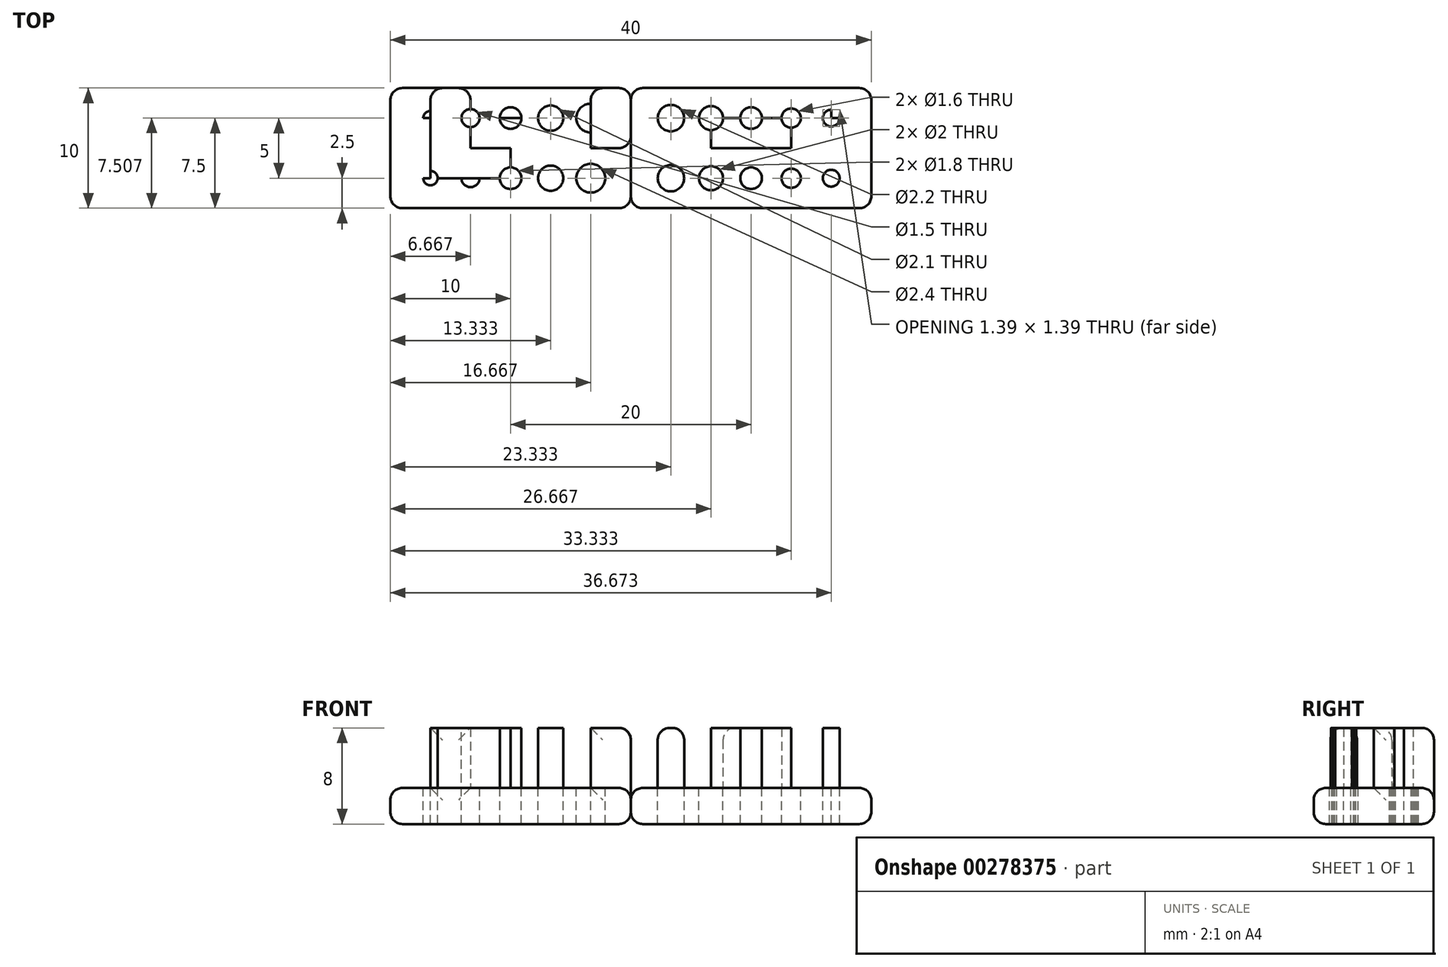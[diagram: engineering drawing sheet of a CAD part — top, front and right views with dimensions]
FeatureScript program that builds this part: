
annotation { "Feature Type Name" : "Feature", "Feature Type Description" : "" }
export const myFeature = defineFeature(function(context is Context, id is Id, definition is map)
    precondition{}
    {
        {
            var Q0;
            Q0=qCreatedBy(makeId("Top.planeOp"),FACE);
            var sketch = newSketch(context, id + "F0", { "sketchPlane" : qUnion([Q0])});
            skLineSegment(sketch, "E0.bottom", {"start": v(10, 2.5) * mm, "end": v(-10, 2.5) * mm});
            skLineSegment(sketch, "E0.top", {"start": v(10, -2.5) * mm, "end": v(-10, -2.5) * mm});
            skLineSegment(sketch, "E0.left", {"start": v(10, 2.5) * mm, "end": v(10, -2.5) * mm});
            skLineSegment(sketch, "E0.right", {"start": v(-10, 2.5) * mm, "end": v(-10, -2.5) * mm});
            skPoint(sketch, "E0.middle", {"position": v(0, 0) * mm});
            skCircle(sketch, "E1", {"center": v(0, 0) * mm, "radius": 0.9 * mm});
            skLineSegment(sketch, "E2", {"start": v(0, 2.5) * mm, "end": v(0, -2.5) * mm});
            skLineSegment(sketch, "E3", {"start": v(-10, 0) * mm, "end": v(10, 0) * mm});
            skLineSegment(sketch, "E4", {"start": v(-6.67, 2.5) * mm, "end": v(-6.67, -2.5) * mm});
            skLineSegment(sketch, "E5", {"start": v(-3.33, 2.5) * mm, "end": v(-3.33, -2.5) * mm});
            skLineSegment(sketch, "E6", {"start": v(3.33, 2.5) * mm, "end": v(3.33, -2.5) * mm});
            skLineSegment(sketch, "E7", {"start": v(6.67, 2.5) * mm, "end": v(6.67, -2.5) * mm});
            skCircle(sketch, "E8", {"center": v(-6.67, 0) * mm, "radius": 0.6 * mm});
            skCircle(sketch, "E9", {"center": v(-3.33, 0) * mm, "radius": 0.75 * mm});
            skCircle(sketch, "E10", {"center": v(3.33, 0) * mm, "radius": 1.05 * mm});
            skCircle(sketch, "E11", {"center": v(6.67, 0) * mm, "radius": 1.2 * mm});
            skLineSegment(sketch, "E12", {"start": v(10, -2.5) * mm, "end": v(10, -7.5) * mm});
            skLineSegment(sketch, "E13", {"start": v(10, -7.5) * mm, "end": v(-10, -7.5) * mm});
            skLineSegment(sketch, "E14", {"start": v(-10, -7.5) * mm, "end": v(-10, -2.5) * mm});
            skLineSegment(sketch, "E15.MirrorCS", {"start": v(-6.67, -7.5) * mm, "end": v(-6.67, -2.5) * mm});
            skLineSegment(sketch, "E16.MirrorCS", {"start": v(-3.33, -7.5) * mm, "end": v(-3.33, -2.5) * mm});
            skLineSegment(sketch, "E17.MirrorCS", {"start": v(0, -7.5) * mm, "end": v(0, -2.5) * mm});
            skLineSegment(sketch, "E18.MirrorCS", {"start": v(3.33, -7.5) * mm, "end": v(3.33, -2.5) * mm});
            skLineSegment(sketch, "E19.MirrorCS", {"start": v(6.67, -7.5) * mm, "end": v(6.67, -2.5) * mm});
            skLineSegment(sketch, "E20.MirrorCS", {"start": v(-10, -5) * mm, "end": v(10, -5) * mm});
            skCircle(sketch, "E21.MirrorC", {"center": v(-6.67, -5) * mm, "radius": 0.6 * mm});
            skCircle(sketch, "E22.MirrorC", {"center": v(-3.33, -5) * mm, "radius": 0.75 * mm});
            skCircle(sketch, "E23.MirrorC", {"center": v(0, -5) * mm, "radius": 0.9 * mm});
            skCircle(sketch, "E24.MirrorC", {"center": v(3.33, -5) * mm, "radius": 1.05 * mm});
            skCircle(sketch, "E25.MirrorC", {"center": v(6.67, -5) * mm, "radius": 1.2 * mm});
            skLineSegment(sketch, "E26.MirrorCS", {"start": v(30, 0) * mm, "end": v(26.67, 0) * mm});
            skLineSegment(sketch, "E27.MirrorCS", {"start": v(10, -2.5) * mm, "end": v(30, -2.5) * mm});
            skLineSegment(sketch, "E28.MirrorCS", {"start": v(10, 2.5) * mm, "end": v(30, 2.5) * mm});
            skLineSegment(sketch, "E29.MirrorCS", {"start": v(30, -5) * mm, "end": v(27.37, -5) * mm});
            skLineSegment(sketch, "E30.MirrorCS", {"start": v(10, -7.5) * mm, "end": v(30, -7.5) * mm});
            skLineSegment(sketch, "E31.MirrorCS", {"start": v(30, -7.5) * mm, "end": v(30, -2.5) * mm});
            skLineSegment(sketch, "E32.MirrorCS", {"start": v(30, 2.5) * mm, "end": v(30, -2.5) * mm});
            skLineSegment(sketch, "E33.MirrorCS", {"start": v(26.67, -5) * mm, "end": v(26.67, -2.5) * mm});
            skLineSegment(sketch, "E34.MirrorCS", {"start": v(20, -7.5) * mm, "end": v(20, -5.9) * mm});
            skLineSegment(sketch, "E35.MirrorCS", {"start": v(16.67, -7.5) * mm, "end": v(16.67, -6) * mm});
            skLineSegment(sketch, "E36.MirrorCS", {"start": v(13.33, -7.5) * mm, "end": v(13.33, -6.1) * mm});
            skLineSegment(sketch, "E37.MirrorCS", {"start": v(13.33, 2.5) * mm, "end": v(13.33, 0) * mm});
            skLineSegment(sketch, "E38.MirrorCS", {"start": v(16.67, 2.5) * mm, "end": v(16.67, 0) * mm});
            skLineSegment(sketch, "E39.MirrorCS", {"start": v(20, 2.5) * mm, "end": v(20, 0) * mm});
            skLineSegment(sketch, "E40.MirrorCS", {"start": v(23.33, 2.5) * mm, "end": v(23.33, 0) * mm});
            skLineSegment(sketch, "E41.MirrorCS", {"start": v(26.67, 2.5) * mm, "end": v(26.67, 0) * mm});
            skCircle(sketch, "E42.MirrorC", {"center": v(26.67, 0) * mm, "radius": 0.7 * mm});
            skCircle(sketch, "E43.MirrorC", {"center": v(23.33, 0) * mm, "radius": 0.8 * mm});
            skCircle(sketch, "E44.MirrorC", {"center": v(20, 0) * mm, "radius": 0.9 * mm});
            skCircle(sketch, "E45.MirrorC", {"center": v(13.33, 0) * mm, "radius": 1.1 * mm});
            skCircle(sketch, "E46.MirrorC", {"center": v(16.67, 0) * mm, "radius": 1 * mm});
            skCircle(sketch, "E47.MirrorC", {"center": v(13.33, -5) * mm, "radius": 1.1 * mm});
            skCircle(sketch, "E48.MirrorC", {"center": v(16.67, -5) * mm, "radius": 1 * mm});
            skCircle(sketch, "E49.MirrorC", {"center": v(20, -5) * mm, "radius": 0.9 * mm});
            skCircle(sketch, "E50.MirrorC", {"center": v(23.33, -5) * mm, "radius": 0.8 * mm});
            skCircle(sketch, "E51.MirrorC", {"center": v(26.67, -5) * mm, "radius": 0.7 * mm});
            skLineSegment(sketch, "E52.trimOffspring", {"start": v(20, -4.1) * mm, "end": v(20, -2.5) * mm});
            skLineSegment(sketch, "E53.trimOffspring", {"start": v(19.1, -5) * mm, "end": v(17.67, -5) * mm});
            skLineSegment(sketch, "E54.trimOffspring", {"start": v(15.67, -5) * mm, "end": v(14.43, -5) * mm});
            skLineSegment(sketch, "E55.trimOffspring", {"start": v(16.67, -5) * mm, "end": v(16.67, -2.5) * mm});
            skLineSegment(sketch, "E56.trimOffspring", {"start": v(12.23, -5) * mm, "end": v(10, -5) * mm});
            skLineSegment(sketch, "E57.trimOffspring", {"start": v(13.33, -5) * mm, "end": v(13.33, -2.5) * mm});
            skLineSegment(sketch, "E58.trimOffspring", {"start": v(13.33, -1.1) * mm, "end": v(13.33, -2.5) * mm});
            skLineSegment(sketch, "E59.trimOffspring", {"start": v(12.23, 0) * mm, "end": v(10, 0) * mm});
            skLineSegment(sketch, "E60.trimOffspring", {"start": v(16.67, -1) * mm, "end": v(16.67, -2.5) * mm});
            skLineSegment(sketch, "E61.trimOffspring", {"start": v(20, -0.9) * mm, "end": v(20, -2.5) * mm});
            skLineSegment(sketch, "E62.trimOffspring", {"start": v(19.1, 0) * mm, "end": v(17.67, 0) * mm});
            skLineSegment(sketch, "E63.trimOffspring", {"start": v(23.33, -0.8) * mm, "end": v(23.33, -2.5) * mm});
            skLineSegment(sketch, "E64.trimOffspring", {"start": v(22.53, 0) * mm, "end": v(20.9, 0) * mm});
            skLineSegment(sketch, "E65.trimOffspring", {"start": v(23.33, -4.2) * mm, "end": v(23.33, -2.5) * mm});
            skPoint(sketch, "E66.MirrorCS.start.orphan", {"position": v(23.33, -7.5) * mm});
            skLineSegment(sketch, "E67.trimOffspring", {"start": v(23.33, -5) * mm, "end": v(20.9, -5) * mm});
            skPoint(sketch, "E68.orphan", {"position": v(26.67, -7.5) * mm});
            skLineSegment(sketch, "E69.trimOffspring", {"start": v(25.97, -5) * mm, "end": v(24.13, -5) * mm});
            skPoint(sketch, "E70.orphan", {"position": v(26.67, -2.5) * mm});
            skLineSegment(sketch, "E71.trimOffspring", {"start": v(25.97, 0) * mm, "end": v(24.13, 0) * mm});
            skSolve(sketch);
        }
        {
            var Q0;
            {var subQ1=sQuery(id+"F0.wireOp",EDGE,"E0.bottom");var subQ5=sQuery(id+"F0.wireOp",EDGE,"E0.left");var subQ6=makeQuery(id+"F0.imprint","INTERSECT",VERTEX,{"derivedFrom":[subQ1,subQ5]});Q0=makeQuery(id+"F0.imprint","IMPRINT",FACE,{"disambiguationData":[TD([[makeQuery(id+"F0.imprint","IMPRINT",EDGE,{"disambiguationData":[TD([[subQ6,-1.0]])],"derivedFrom":subQ1}),1.0]])]});}
            var Q1;
            {var subQ1=sQuery(id+"F0.wireOp",EDGE,"E0.bottom");var subQ6=sQuery(id+"F0.wireOp",EDGE,"E0.right");var subQ9=makeQuery(id+"F0.imprint","INTERSECT",VERTEX,{"derivedFrom":[subQ1,subQ6]});Q1=makeQuery(id+"F0.imprint","IMPRINT",FACE,{"disambiguationData":[TD([[makeQuery(id+"F0.imprint","IMPRINT",EDGE,{"disambiguationData":[TD([[subQ9,1.0]])],"derivedFrom":subQ1}),1.0]])]});}
            var Q2;
            {var subQ1=sQuery(id+"F0.wireOp",EDGE,"E12");var subQ6=sQuery(id+"F0.wireOp",EDGE,"E13");var subQ9=makeQuery(id+"F0.imprint","INTERSECT",VERTEX,{"derivedFrom":[subQ1,subQ6]});Q2=makeQuery(id+"F0.imprint","IMPRINT",FACE,{"disambiguationData":[TD([[makeQuery(id+"F0.imprint","IMPRINT",EDGE,{"disambiguationData":[TD([[subQ9,1.0]])],"derivedFrom":subQ1}),-1.0]])]});}
            var Q3;
            {var subQ1=sQuery(id+"F0.wireOp",EDGE,"E14");var subQ6=sQuery(id+"F0.wireOp",EDGE,"E13");var subQ9=makeQuery(id+"F0.imprint","INTERSECT",VERTEX,{"derivedFrom":[subQ6,subQ1]});Q3=makeQuery(id+"F0.imprint","IMPRINT",FACE,{"disambiguationData":[TD([[makeQuery(id+"F0.imprint","IMPRINT",EDGE,{"disambiguationData":[TD([[subQ9,1.0]])],"derivedFrom":subQ6}),-1.0]])]});}
            var Q4;
            {var subQ5=sQuery(id+"F0.wireOp",EDGE,"E3");var subQ6=sQuery(id+"F0.wireOp",EDGE,"E0.left");var subQ7=makeQuery(id+"F0.imprint","INTERSECT",VERTEX,{"derivedFrom":[subQ6,subQ5]});Q4=makeQuery(id+"F0.imprint","IMPRINT",FACE,{"disambiguationData":[TD([[makeQuery(id+"F0.imprint","IMPRINT",EDGE,{"disambiguationData":[TD([[subQ7,1.0]])],"derivedFrom":subQ5}),-1.0]])]});}
            var Q5;
            {var subQ5=sQuery(id+"F0.wireOp",EDGE,"E12");var subQ7=sQuery(id+"F0.wireOp",EDGE,"E20.MirrorCS");var subQ8=makeQuery(id+"F0.imprint","INTERSECT",VERTEX,{"derivedFrom":[subQ5,subQ7]});Q5=makeQuery(id+"F0.imprint","IMPRINT",FACE,{"disambiguationData":[TD([[makeQuery(id+"F0.imprint","IMPRINT",EDGE,{"disambiguationData":[TD([[subQ8,1.0]])],"derivedFrom":subQ7}),1.0]])]});}
            var Q6;
            {var subQ5=sQuery(id+"F0.wireOp",EDGE,"E0.right");var subQ7=sQuery(id+"F0.wireOp",EDGE,"E3");var subQ8=makeQuery(id+"F0.imprint","INTERSECT",VERTEX,{"derivedFrom":[subQ5,subQ7]});Q6=makeQuery(id+"F0.imprint","IMPRINT",FACE,{"disambiguationData":[TD([[makeQuery(id+"F0.imprint","IMPRINT",EDGE,{"disambiguationData":[TD([[subQ8,-1.0]])],"derivedFrom":subQ7}),-1.0]])]});}
            var Q7;
            {var subQ5=sQuery(id+"F0.wireOp",EDGE,"E20.MirrorCS");var subQ6=sQuery(id+"F0.wireOp",EDGE,"E14");var subQ7=makeQuery(id+"F0.imprint","INTERSECT",VERTEX,{"derivedFrom":[subQ6,subQ5]});Q7=makeQuery(id+"F0.imprint","IMPRINT",FACE,{"disambiguationData":[TD([[makeQuery(id+"F0.imprint","IMPRINT",EDGE,{"disambiguationData":[TD([[subQ7,-1.0]])],"derivedFrom":subQ5}),1.0]])]});}
            var Q8;
            {var subQ1=sQuery(id+"F0.wireOp",EDGE,"E0.bottom");var subQ5=sQuery(id+"F0.wireOp",EDGE,"E6");var subQ6=makeQuery(id+"F0.imprint","INTERSECT",VERTEX,{"derivedFrom":[subQ1,subQ5]});Q8=makeQuery(id+"F0.imprint","IMPRINT",FACE,{"disambiguationData":[TD([[makeQuery(id+"F0.imprint","IMPRINT",EDGE,{"disambiguationData":[TD([[subQ6,1.0]])],"derivedFrom":subQ1}),1.0]])]});}
            var Q9;
            {var subQ0=sQuery(id+"F0.wireOp",EDGE,"E2");var subQ1=sQuery(id+"F0.wireOp",EDGE,"E0.bottom");var subQ2=makeQuery(id+"F0.imprint","INTERSECT",VERTEX,{"derivedFrom":[subQ1,subQ0]});Q9=makeQuery(id+"F0.imprint","IMPRINT",FACE,{"disambiguationData":[TD([[makeQuery(id+"F0.imprint","IMPRINT",EDGE,{"disambiguationData":[TD([[subQ2,1.0]])],"derivedFrom":subQ1}),1.0]])]});}
            var Q10;
            {var subQ5=sQuery(id+"F0.wireOp",EDGE,"E2");var subQ6=sQuery(id+"F0.wireOp",EDGE,"E0.bottom");var subQ7=makeQuery(id+"F0.imprint","INTERSECT",VERTEX,{"derivedFrom":[subQ6,subQ5]});Q10=makeQuery(id+"F0.imprint","IMPRINT",FACE,{"disambiguationData":[TD([[makeQuery(id+"F0.imprint","IMPRINT",EDGE,{"disambiguationData":[TD([[subQ7,-1.0]])],"derivedFrom":subQ6}),1.0]])]});}
            var Q11;
            {var subQ0=sQuery(id+"F0.wireOp",EDGE,"E4");var subQ1=sQuery(id+"F0.wireOp",EDGE,"E0.bottom");var subQ2=makeQuery(id+"F0.imprint","INTERSECT",VERTEX,{"derivedFrom":[subQ1,subQ0]});Q11=makeQuery(id+"F0.imprint","IMPRINT",FACE,{"disambiguationData":[TD([[makeQuery(id+"F0.imprint","IMPRINT",EDGE,{"disambiguationData":[TD([[subQ2,1.0]])],"derivedFrom":subQ1}),1.0]])]});}
            var Q12;
            {var subQ5=sQuery(id+"F0.wireOp",EDGE,"E17.MirrorCS");var subQ6=sQuery(id+"F0.wireOp",EDGE,"E13");var subQ7=makeQuery(id+"F0.imprint","INTERSECT",VERTEX,{"derivedFrom":[subQ6,subQ5]});Q12=makeQuery(id+"F0.imprint","IMPRINT",FACE,{"disambiguationData":[TD([[makeQuery(id+"F0.imprint","IMPRINT",EDGE,{"disambiguationData":[TD([[subQ7,1.0]])],"derivedFrom":subQ6}),-1.0]])]});}
            var Q13;
            {var subQ7=sQuery(id+"F0.wireOp",EDGE,"E13");var subQ9=sQuery(id+"F0.wireOp",EDGE,"E15.MirrorCS");var subQ10=makeQuery(id+"F0.imprint","INTERSECT",VERTEX,{"derivedFrom":[subQ7,subQ9]});Q13=makeQuery(id+"F0.imprint","IMPRINT",FACE,{"disambiguationData":[TD([[makeQuery(id+"F0.imprint","IMPRINT",EDGE,{"disambiguationData":[TD([[subQ10,1.0]])],"derivedFrom":subQ7}),-1.0]])]});}
            var Q14;
            {var subQ7=sQuery(id+"F0.wireOp",EDGE,"E10");var subQ9=sQuery(id+"F0.wireOp",EDGE,"E3");var subQ10=makeQuery(id+"F0.imprint","INTERSECT",VERTEX,{"disambiguationData":[OD(1.0)],"derivedFrom":[subQ9,subQ7]});Q14=makeQuery(id+"F0.imprint","IMPRINT",FACE,{"disambiguationData":[TD([[makeQuery(id+"F0.imprint","IMPRINT",EDGE,{"disambiguationData":[TD([[subQ10,-1.0]])],"derivedFrom":subQ9}),-1.0]])]});}
            var Q15;
            {var subQ0=sQuery(id+"F0.wireOp",EDGE,"E3");var subQ1=sQuery(id+"F0.wireOp",EDGE,"E1");var subQ2=makeQuery(id+"F0.imprint","INTERSECT",VERTEX,{"disambiguationData":[OD(0.0)],"derivedFrom":[subQ1,subQ0]});Q15=makeQuery(id+"F0.imprint","IMPRINT",FACE,{"disambiguationData":[TD([[makeQuery(id+"F0.imprint","IMPRINT",EDGE,{"disambiguationData":[TD([[subQ2,1.0]])],"derivedFrom":subQ1}),-1.0]])]});}
            var Q16;
            {var subQ0=sQuery(id+"F0.wireOp",EDGE,"E3");var subQ1=sQuery(id+"F0.wireOp",EDGE,"E1");var subQ2=makeQuery(id+"F0.imprint","INTERSECT",VERTEX,{"disambiguationData":[OD(1.0)],"derivedFrom":[subQ1,subQ0]});Q16=makeQuery(id+"F0.imprint","IMPRINT",FACE,{"disambiguationData":[TD([[makeQuery(id+"F0.imprint","IMPRINT",EDGE,{"disambiguationData":[TD([[subQ2,-1.0]])],"derivedFrom":subQ1}),-1.0]])]});}
            var Q17;
            {var subQ7=sQuery(id+"F0.wireOp",EDGE,"E8");var subQ9=sQuery(id+"F0.wireOp",EDGE,"E3");var subQ10=makeQuery(id+"F0.imprint","INTERSECT",VERTEX,{"disambiguationData":[OD(1.0)],"derivedFrom":[subQ9,subQ7]});Q17=makeQuery(id+"F0.imprint","IMPRINT",FACE,{"disambiguationData":[TD([[makeQuery(id+"F0.imprint","IMPRINT",EDGE,{"disambiguationData":[TD([[subQ10,-1.0]])],"derivedFrom":subQ9}),-1.0]])]});}
            var Q18;
            {var subQ0=sQuery(id+"F0.wireOp",EDGE,"E22.MirrorC");var subQ1=sQuery(id+"F0.wireOp",EDGE,"E20.MirrorCS");var subQ2=makeQuery(id+"F0.imprint","INTERSECT",VERTEX,{"disambiguationData":[OD(1.0)],"derivedFrom":[subQ1,subQ0]});Q18=makeQuery(id+"F0.imprint","IMPRINT",FACE,{"disambiguationData":[TD([[makeQuery(id+"F0.imprint","IMPRINT",EDGE,{"disambiguationData":[TD([[subQ2,-1.0]])],"derivedFrom":subQ1}),1.0]])]});}
            var Q19;
            {var subQ5=sQuery(id+"F0.wireOp",EDGE,"E23.MirrorC");var subQ6=sQuery(id+"F0.wireOp",EDGE,"E20.MirrorCS");var subQ7=makeQuery(id+"F0.imprint","INTERSECT",VERTEX,{"disambiguationData":[OD(1.0)],"derivedFrom":[subQ6,subQ5]});Q19=makeQuery(id+"F0.imprint","IMPRINT",FACE,{"disambiguationData":[TD([[makeQuery(id+"F0.imprint","IMPRINT",EDGE,{"disambiguationData":[TD([[subQ7,-1.0]])],"derivedFrom":subQ6}),1.0]])]});}
            var Q20;
            {var subQ0=sQuery(id+"F0.wireOp",EDGE,"E24.MirrorC");var subQ1=sQuery(id+"F0.wireOp",EDGE,"E20.MirrorCS");var subQ2=makeQuery(id+"F0.imprint","INTERSECT",VERTEX,{"disambiguationData":[OD(1.0)],"derivedFrom":[subQ1,subQ0]});Q20=makeQuery(id+"F0.imprint","IMPRINT",FACE,{"disambiguationData":[TD([[makeQuery(id+"F0.imprint","IMPRINT",EDGE,{"disambiguationData":[TD([[subQ2,-1.0]])],"derivedFrom":subQ1}),1.0]])]});}
            var Q21;
            {var subQ6=sQuery(id+"F0.wireOp",EDGE,"E13");var subQ9=sQuery(id+"F0.wireOp",EDGE,"E18.MirrorCS");var subQ10=makeQuery(id+"F0.imprint","INTERSECT",VERTEX,{"derivedFrom":[subQ6,subQ9]});Q21=makeQuery(id+"F0.imprint","IMPRINT",FACE,{"disambiguationData":[TD([[makeQuery(id+"F0.imprint","IMPRINT",EDGE,{"disambiguationData":[TD([[subQ10,1.0]])],"derivedFrom":subQ6}),-1.0]])]});}
            var Q22;
            {var subQ1=sQuery(id+"F0.wireOp",EDGE,"E13");var subQ9=sQuery(id+"F0.wireOp",EDGE,"E16.MirrorCS");var subQ10=makeQuery(id+"F0.imprint","INTERSECT",VERTEX,{"derivedFrom":[subQ1,subQ9]});Q22=makeQuery(id+"F0.imprint","IMPRINT",FACE,{"disambiguationData":[TD([[makeQuery(id+"F0.imprint","IMPRINT",EDGE,{"disambiguationData":[TD([[subQ10,1.0]])],"derivedFrom":subQ1}),-1.0]])]});}
            var Q23;
            {var subQ0=sQuery(id+"F0.wireOp",EDGE,"E8");var subQ1=sQuery(id+"F0.wireOp",EDGE,"E3");var subQ2=makeQuery(id+"F0.imprint","INTERSECT",VERTEX,{"disambiguationData":[OD(0.0)],"derivedFrom":[subQ1,subQ0]});Q23=makeQuery(id+"F0.imprint","IMPRINT",FACE,{"disambiguationData":[TD([[makeQuery(id+"F0.imprint","IMPRINT",EDGE,{"disambiguationData":[TD([[subQ2,-1.0]])],"derivedFrom":subQ1}),-1.0]])]});}
            var Q24;
            {var subQ0=sQuery(id+"F0.wireOp",EDGE,"E4");var subQ1=sQuery(id+"F0.wireOp",EDGE,"E3");var subQ2=makeQuery(id+"F0.imprint","INTERSECT",VERTEX,{"derivedFrom":[subQ1,subQ0]});Q24=makeQuery(id+"F0.imprint","IMPRINT",FACE,{"disambiguationData":[TD([[makeQuery(id+"F0.imprint","IMPRINT",EDGE,{"disambiguationData":[TD([[subQ2,-1.0]])],"derivedFrom":subQ1}),-1.0]])]});}
            var Q25;
            {var subQ0=sQuery(id+"F0.wireOp",EDGE,"E4");var subQ1=sQuery(id+"F0.wireOp",EDGE,"E3");var subQ2=makeQuery(id+"F0.imprint","INTERSECT",VERTEX,{"derivedFrom":[subQ1,subQ0]});Q25=makeQuery(id+"F0.imprint","IMPRINT",FACE,{"disambiguationData":[TD([[makeQuery(id+"F0.imprint","IMPRINT",EDGE,{"disambiguationData":[TD([[subQ2,-1.0]])],"derivedFrom":subQ1}),1.0]])]});}
            var Q26;
            {var subQ0=sQuery(id+"F0.wireOp",EDGE,"E8");var subQ1=sQuery(id+"F0.wireOp",EDGE,"E3");var subQ2=makeQuery(id+"F0.imprint","INTERSECT",VERTEX,{"disambiguationData":[OD(0.0)],"derivedFrom":[subQ1,subQ0]});Q26=makeQuery(id+"F0.imprint","IMPRINT",FACE,{"disambiguationData":[TD([[makeQuery(id+"F0.imprint","IMPRINT",EDGE,{"disambiguationData":[TD([[subQ2,-1.0]])],"derivedFrom":subQ1}),1.0]])]});}
            var Q27;
            {var subQ0=sQuery(id+"F0.wireOp",EDGE,"E2");var subQ1=sQuery(id+"F0.wireOp",EDGE,"E1");var subQ2=makeQuery(id+"F0.imprint","INTERSECT",VERTEX,{"disambiguationData":[OD(0.0)],"derivedFrom":[subQ1,subQ0]});Q27=makeQuery(id+"F0.imprint","IMPRINT",FACE,{"disambiguationData":[TD([[makeQuery(id+"F0.imprint","IMPRINT",EDGE,{"disambiguationData":[TD([[subQ2,-1.0]])],"derivedFrom":subQ1}),1.0]])]});}
            var Q28;
            {var subQ0=sQuery(id+"F0.wireOp",EDGE,"E3");var subQ1=sQuery(id+"F0.wireOp",EDGE,"E1");var subQ2=makeQuery(id+"F0.imprint","INTERSECT",VERTEX,{"disambiguationData":[OD(0.0)],"derivedFrom":[subQ1,subQ0]});Q28=makeQuery(id+"F0.imprint","IMPRINT",FACE,{"disambiguationData":[TD([[makeQuery(id+"F0.imprint","IMPRINT",EDGE,{"disambiguationData":[TD([[subQ2,1.0]])],"derivedFrom":subQ1}),1.0]])]});}
            var Q29;
            {var subQ0=sQuery(id+"F0.wireOp",EDGE,"E2");var subQ1=sQuery(id+"F0.wireOp",EDGE,"E1");var subQ2=makeQuery(id+"F0.imprint","INTERSECT",VERTEX,{"disambiguationData":[OD(0.0)],"derivedFrom":[subQ1,subQ0]});Q29=makeQuery(id+"F0.imprint","IMPRINT",FACE,{"disambiguationData":[TD([[makeQuery(id+"F0.imprint","IMPRINT",EDGE,{"disambiguationData":[TD([[subQ2,1.0]])],"derivedFrom":subQ1}),1.0]])]});}
            var Q30;
            {var subQ0=sQuery(id+"F0.wireOp",EDGE,"E7");var subQ1=sQuery(id+"F0.wireOp",EDGE,"E3");var subQ2=makeQuery(id+"F0.imprint","INTERSECT",VERTEX,{"derivedFrom":[subQ1,subQ0]});Q30=makeQuery(id+"F0.imprint","IMPRINT",FACE,{"disambiguationData":[TD([[makeQuery(id+"F0.imprint","IMPRINT",EDGE,{"disambiguationData":[TD([[subQ2,-1.0]])],"derivedFrom":subQ1}),1.0]])]});}
            var Q31;
            {var subQ0=sQuery(id+"F0.wireOp",EDGE,"E7");var subQ1=sQuery(id+"F0.wireOp",EDGE,"E3");var subQ2=makeQuery(id+"F0.imprint","INTERSECT",VERTEX,{"derivedFrom":[subQ1,subQ0]});Q31=makeQuery(id+"F0.imprint","IMPRINT",FACE,{"disambiguationData":[TD([[makeQuery(id+"F0.imprint","IMPRINT",EDGE,{"disambiguationData":[TD([[subQ2,-1.0]])],"derivedFrom":subQ1}),-1.0]])]});}
            var Q32;
            {var subQ0=sQuery(id+"F0.wireOp",EDGE,"E11");var subQ1=sQuery(id+"F0.wireOp",EDGE,"E3");var subQ2=makeQuery(id+"F0.imprint","INTERSECT",VERTEX,{"disambiguationData":[OD(0.0)],"derivedFrom":[subQ1,subQ0]});Q32=makeQuery(id+"F0.imprint","IMPRINT",FACE,{"disambiguationData":[TD([[makeQuery(id+"F0.imprint","IMPRINT",EDGE,{"disambiguationData":[TD([[subQ2,-1.0]])],"derivedFrom":subQ1}),-1.0]])]});}
            var Q33;
            {var subQ0=sQuery(id+"F0.wireOp",EDGE,"E11");var subQ1=sQuery(id+"F0.wireOp",EDGE,"E3");var subQ2=makeQuery(id+"F0.imprint","INTERSECT",VERTEX,{"disambiguationData":[OD(0.0)],"derivedFrom":[subQ1,subQ0]});Q33=makeQuery(id+"F0.imprint","IMPRINT",FACE,{"disambiguationData":[TD([[makeQuery(id+"F0.imprint","IMPRINT",EDGE,{"disambiguationData":[TD([[subQ2,-1.0]])],"derivedFrom":subQ1}),1.0]])]});}
            var Q34;
            {var subQ0=sQuery(id+"F0.wireOp",EDGE,"E3");var subQ1=sQuery(id+"F0.wireOp",EDGE,"E1");var subQ2=makeQuery(id+"F0.imprint","INTERSECT",VERTEX,{"disambiguationData":[OD(1.0)],"derivedFrom":[subQ1,subQ0]});Q34=makeQuery(id+"F0.imprint","IMPRINT",FACE,{"disambiguationData":[TD([[makeQuery(id+"F0.imprint","IMPRINT",EDGE,{"disambiguationData":[TD([[subQ2,-1.0]])],"derivedFrom":subQ1}),1.0]])]});}
            var Q35;
            {var subQ0=sQuery(id+"F0.wireOp",EDGE,"E24.MirrorC");var subQ1=sQuery(id+"F0.wireOp",EDGE,"E18.MirrorCS");var subQ2=makeQuery(id+"F0.imprint","INTERSECT",VERTEX,{"disambiguationData":[OD(0.0)],"derivedFrom":[subQ1,subQ0]});Q35=makeQuery(id+"F0.imprint","IMPRINT",FACE,{"disambiguationData":[TD([[makeQuery(id+"F0.imprint","IMPRINT",EDGE,{"disambiguationData":[TD([[subQ2,-1.0]])],"derivedFrom":subQ1}),1.0]])]});}
            var Q36;
            {var subQ0=sQuery(id+"F0.wireOp",EDGE,"E20.MirrorCS");var subQ1=sQuery(id+"F0.wireOp",EDGE,"E18.MirrorCS");var subQ2=makeQuery(id+"F0.imprint","INTERSECT",VERTEX,{"derivedFrom":[subQ1,subQ0]});Q36=makeQuery(id+"F0.imprint","IMPRINT",FACE,{"disambiguationData":[TD([[makeQuery(id+"F0.imprint","IMPRINT",EDGE,{"disambiguationData":[TD([[subQ2,-1.0]])],"derivedFrom":subQ1}),1.0]])]});}
            var Q37;
            {var subQ0=sQuery(id+"F0.wireOp",EDGE,"E20.MirrorCS");var subQ1=sQuery(id+"F0.wireOp",EDGE,"E18.MirrorCS");var subQ2=makeQuery(id+"F0.imprint","INTERSECT",VERTEX,{"derivedFrom":[subQ1,subQ0]});Q37=makeQuery(id+"F0.imprint","IMPRINT",FACE,{"disambiguationData":[TD([[makeQuery(id+"F0.imprint","IMPRINT",EDGE,{"disambiguationData":[TD([[subQ2,-1.0]])],"derivedFrom":subQ1}),-1.0]])]});}
            var Q38;
            {var subQ0=sQuery(id+"F0.wireOp",EDGE,"E24.MirrorC");var subQ1=sQuery(id+"F0.wireOp",EDGE,"E18.MirrorCS");var subQ2=makeQuery(id+"F0.imprint","INTERSECT",VERTEX,{"disambiguationData":[OD(0.0)],"derivedFrom":[subQ1,subQ0]});Q38=makeQuery(id+"F0.imprint","IMPRINT",FACE,{"disambiguationData":[TD([[makeQuery(id+"F0.imprint","IMPRINT",EDGE,{"disambiguationData":[TD([[subQ2,-1.0]])],"derivedFrom":subQ1}),-1.0]])]});}
            var Q39;
            {var subQ0=sQuery(id+"F0.wireOp",EDGE,"E22.MirrorC");var subQ1=sQuery(id+"F0.wireOp",EDGE,"E16.MirrorCS");var subQ2=makeQuery(id+"F0.imprint","INTERSECT",VERTEX,{"disambiguationData":[OD(0.0)],"derivedFrom":[subQ1,subQ0]});Q39=makeQuery(id+"F0.imprint","IMPRINT",FACE,{"disambiguationData":[TD([[makeQuery(id+"F0.imprint","IMPRINT",EDGE,{"disambiguationData":[TD([[subQ2,-1.0]])],"derivedFrom":subQ1}),-1.0]])]});}
            var Q40;
            {var subQ0=sQuery(id+"F0.wireOp",EDGE,"E22.MirrorC");var subQ1=sQuery(id+"F0.wireOp",EDGE,"E16.MirrorCS");var subQ2=makeQuery(id+"F0.imprint","INTERSECT",VERTEX,{"disambiguationData":[OD(0.0)],"derivedFrom":[subQ1,subQ0]});Q40=makeQuery(id+"F0.imprint","IMPRINT",FACE,{"disambiguationData":[TD([[makeQuery(id+"F0.imprint","IMPRINT",EDGE,{"disambiguationData":[TD([[subQ2,-1.0]])],"derivedFrom":subQ1}),1.0]])]});}
            var Q41;
            {var subQ0=sQuery(id+"F0.wireOp",EDGE,"E20.MirrorCS");var subQ1=sQuery(id+"F0.wireOp",EDGE,"E16.MirrorCS");var subQ2=makeQuery(id+"F0.imprint","INTERSECT",VERTEX,{"derivedFrom":[subQ1,subQ0]});Q41=makeQuery(id+"F0.imprint","IMPRINT",FACE,{"disambiguationData":[TD([[makeQuery(id+"F0.imprint","IMPRINT",EDGE,{"disambiguationData":[TD([[subQ2,-1.0]])],"derivedFrom":subQ1}),-1.0]])]});}
            var Q42;
            {var subQ0=sQuery(id+"F0.wireOp",EDGE,"E21.MirrorC");var subQ1=sQuery(id+"F0.wireOp",EDGE,"E20.MirrorCS");var subQ2=makeQuery(id+"F0.imprint","INTERSECT",VERTEX,{"disambiguationData":[OD(1.0)],"derivedFrom":[subQ1,subQ0]});Q42=makeQuery(id+"F0.imprint","IMPRINT",FACE,{"disambiguationData":[TD([[makeQuery(id+"F0.imprint","IMPRINT",EDGE,{"disambiguationData":[TD([[subQ2,-1.0]])],"derivedFrom":subQ1}),1.0]])]});}
            var Q43;
            {var subQ0=sQuery(id+"F0.wireOp",EDGE,"E20.MirrorCS");var subQ1=sQuery(id+"F0.wireOp",EDGE,"E16.MirrorCS");var subQ2=makeQuery(id+"F0.imprint","INTERSECT",VERTEX,{"derivedFrom":[subQ1,subQ0]});Q43=makeQuery(id+"F0.imprint","IMPRINT",FACE,{"disambiguationData":[TD([[makeQuery(id+"F0.imprint","IMPRINT",EDGE,{"disambiguationData":[TD([[subQ2,-1.0]])],"derivedFrom":subQ1}),1.0]])]});}
            var Q44;
            {var subQ0=sQuery(id+"F0.wireOp",EDGE,"b7081483-e7ee-48de-b9ec-7c7101615ecb.sketch_text.stroke-19");Q44=makeQuery(id+"F0.imprint","IMPRINT",FACE,{"disambiguationData":[TD([[makeQuery(id+"F0.imprint","IMPRINT",EDGE,{"derivedFrom":subQ0}),-1.0]])]});}
            var Q45;
            Q45=makeQuery(id+"F0.imprint","IMPRINT",FACE,{"disambiguationData":[TD([[makeQuery(id+"F0.imprint","IMPRINT",EDGE,{"derivedFrom":sQuery(id+"F0.wireOp",EDGE,"b7081483-e7ee-48de-b9ec-7c7101615ecb.sketch_text.stroke-41")}),1.0]])]});
            var Q46;
            Q46=makeQuery(id+"F0.imprint","IMPRINT",FACE,{"disambiguationData":[TD([[makeQuery(id+"F0.imprint","IMPRINT",EDGE,{"derivedFrom":sQuery(id+"F0.wireOp",EDGE,"b7081483-e7ee-48de-b9ec-7c7101615ecb.sketch_text.stroke-34")}),1.0]])]});
            var Q47;
            Q47=makeQuery(id+"F0.imprint","IMPRINT",FACE,{"disambiguationData":[TD([[makeQuery(id+"F0.imprint","IMPRINT",EDGE,{"derivedFrom":sQuery(id+"F0.wireOp",EDGE,"b7081483-e7ee-48de-b9ec-7c7101615ecb.sketch_text.stroke-10")}),-1.0]])]});
            var Q48;
            Q48=makeQuery(id+"F0.imprint","IMPRINT",FACE,{"disambiguationData":[TD([[makeQuery(id+"F0.imprint","IMPRINT",EDGE,{"derivedFrom":sQuery(id+"F0.wireOp",EDGE,"b7081483-e7ee-48de-b9ec-7c7101615ecb.sketch_text.stroke-0")}),-1.0]])]});
            var Q49;
            {var subQ0=sQuery(id+"F0.wireOp",EDGE,"b7081483-e7ee-48de-b9ec-7c7101615ecb.sketch_text.stroke-13");Q49=makeQuery(id+"F0.imprint","IMPRINT",FACE,{"disambiguationData":[TD([[makeQuery(id+"F0.imprint","IMPRINT",EDGE,{"derivedFrom":subQ0}),-1.0]])]});}
            var Q50;
            Q50=makeQuery(id+"F0.imprint","IMPRINT",FACE,{"disambiguationData":[TD([[makeQuery(id+"F0.imprint","IMPRINT",EDGE,{"derivedFrom":sQuery(id+"F0.wireOp",EDGE,"efd9baf5-7fcf-4915-bd8e-df319a8cdb6d.sketch_text.stroke-0")}),-1.0]])]});
            var Q51;
            {var subQ0=sQuery(id+"F0.wireOp",EDGE,"efd9baf5-7fcf-4915-bd8e-df319a8cdb6d.sketch_text.stroke-26");Q51=makeQuery(id+"F0.imprint","IMPRINT",FACE,{"disambiguationData":[TD([[makeQuery(id+"F0.imprint","IMPRINT",EDGE,{"derivedFrom":subQ0}),-1.0]])]});}
            var Q52;
            {var subQ5=sQuery(id+"F0.wireOp",EDGE,"efd9baf5-7fcf-4915-bd8e-df319a8cdb6d.sketch_text.stroke-24");Q52=makeQuery(id+"F0.imprint","IMPRINT",FACE,{"disambiguationData":[TD([[makeQuery(id+"F0.imprint","IMPRINT",EDGE,{"derivedFrom":subQ5}),-1.0]])]});}
            var Q53;
            Q53=makeQuery(id+"F0.imprint","IMPRINT",FACE,{"disambiguationData":[TD([[makeQuery(id+"F0.imprint","IMPRINT",EDGE,{"derivedFrom":sQuery(id+"F0.wireOp",EDGE,"efd9baf5-7fcf-4915-bd8e-df319a8cdb6d.sketch_text.stroke-32")}),-1.0]])]});
            var Q54;
            Q54=makeQuery(id+"F0.imprint","IMPRINT",FACE,{"disambiguationData":[TD([[makeQuery(id+"F0.imprint","IMPRINT",EDGE,{"derivedFrom":sQuery(id+"F0.wireOp",EDGE,"6840c35f-97e4-48b3-a313-5b88f69b1126.sketch_text.stroke-18")}),-1.0]])]});
            var Q55;
            Q55=makeQuery(id+"F0.imprint","IMPRINT",FACE,{"disambiguationData":[TD([[makeQuery(id+"F0.imprint","IMPRINT",EDGE,{"derivedFrom":sQuery(id+"F0.wireOp",EDGE,"6840c35f-97e4-48b3-a313-5b88f69b1126.sketch_text.stroke-10")}),-1.0]])]});
            var Q56;
            Q56=makeQuery(id+"F0.imprint","IMPRINT",FACE,{"disambiguationData":[TD([[makeQuery(id+"F0.imprint","IMPRINT",EDGE,{"derivedFrom":sQuery(id+"F0.wireOp",EDGE,"6840c35f-97e4-48b3-a313-5b88f69b1126.sketch_text.stroke-0")}),-1.0]])]});
            var Q57;
            {var subQ6=sQuery(id+"F0.wireOp",EDGE,"6840c35f-97e4-48b3-a313-5b88f69b1126.sketch_text.stroke-13");Q57=makeQuery(id+"F0.imprint","IMPRINT",FACE,{"disambiguationData":[TD([[makeQuery(id+"F0.imprint","IMPRINT",EDGE,{"derivedFrom":subQ6}),-1.0]])]});}
            var Q58;
            Q58=makeQuery(id+"F0.imprint","IMPRINT",FACE,{"disambiguationData":[TD([[makeQuery(id+"F0.imprint","IMPRINT",EDGE,{"derivedFrom":sQuery(id+"F0.wireOp",EDGE,"d91866c6-2488-4bc1-93d3-df7be0e70187.sketch_text.stroke-18")}),-1.0]])]});
            var Q59;
            Q59=makeQuery(id+"F0.imprint","IMPRINT",FACE,{"disambiguationData":[TD([[makeQuery(id+"F0.imprint","IMPRINT",EDGE,{"derivedFrom":sQuery(id+"F0.wireOp",EDGE,"d91866c6-2488-4bc1-93d3-df7be0e70187.sketch_text.stroke-0")}),-1.0]])]});
            var Q60;
            Q60=makeQuery(id+"F0.imprint","IMPRINT",FACE,{"disambiguationData":[TD([[makeQuery(id+"F0.imprint","IMPRINT",EDGE,{"derivedFrom":sQuery(id+"F0.wireOp",EDGE,"d91866c6-2488-4bc1-93d3-df7be0e70187.sketch_text.stroke-10")}),-1.0]])]});
            var Q61;
            {var subQ1=sQuery(id+"F0.wireOp",EDGE,"d91866c6-2488-4bc1-93d3-df7be0e70187.sketch_text.stroke-13");Q61=makeQuery(id+"F0.imprint","IMPRINT",FACE,{"disambiguationData":[TD([[makeQuery(id+"F0.imprint","IMPRINT",EDGE,{"derivedFrom":subQ1}),-1.0]])]});}
            var Q62;
            Q62=makeQuery(id+"F0.imprint","IMPRINT",FACE,{"disambiguationData":[TD([[makeQuery(id+"F0.imprint","IMPRINT",EDGE,{"derivedFrom":sQuery(id+"F0.wireOp",EDGE,"c46f5712-8b37-4575-8038-2aa2820e6cab.sketch_text.stroke-32")}),-1.0]])]});
            var Q63;
            Q63=makeQuery(id+"F0.imprint","IMPRINT",FACE,{"disambiguationData":[TD([[makeQuery(id+"F0.imprint","IMPRINT",EDGE,{"derivedFrom":sQuery(id+"F0.wireOp",EDGE,"c46f5712-8b37-4575-8038-2aa2820e6cab.sketch_text.stroke-0")}),-1.0]])]});
            var Q64;
            Q64=makeQuery(id+"F0.imprint","IMPRINT",FACE,{"disambiguationData":[TD([[makeQuery(id+"F0.imprint","IMPRINT",EDGE,{"derivedFrom":sQuery(id+"F0.wireOp",EDGE,"c46f5712-8b37-4575-8038-2aa2820e6cab.sketch_text.stroke-24")}),-1.0]])]});
            var Q65;
            {var subQ1=sQuery(id+"F0.wireOp",EDGE,"c46f5712-8b37-4575-8038-2aa2820e6cab.sketch_text.stroke-27");Q65=makeQuery(id+"F0.imprint","IMPRINT",FACE,{"disambiguationData":[TD([[makeQuery(id+"F0.imprint","IMPRINT",EDGE,{"derivedFrom":subQ1}),-1.0]])]});}
            var Q66;
            Q66=makeQuery(id+"F0.imprint","IMPRINT",FACE,{"disambiguationData":[TD([[makeQuery(id+"F0.imprint","IMPRINT",EDGE,{"derivedFrom":sQuery(id+"F0.wireOp",EDGE,"c46f5712-8b37-4575-8038-2aa2820e6cab.sketch_text.stroke-43")}),1.0]])]});
            extrude(context, id + "F1", {"entities" : qUnion([Q0, Q1, Q2, Q3, Q4, Q5, Q6, Q7, Q8, Q9, Q10, Q11, Q12, Q13, Q14, Q15, Q16, Q17, Q18, Q19, Q20, Q21, Q22, Q23, Q24, Q25, Q26, Q27, Q28, Q29, Q30, Q31, Q32, Q33, Q34, Q35, Q36, Q37, Q38, Q39, Q40, Q41, Q42, Q43, Q44, Q45, Q46, Q47, Q48, Q49, Q50, Q51, Q52, Q53, Q54, Q55, Q56, Q57, Q58, Q59, Q60, Q61, Q62, Q63, Q64, Q65, Q66]), "oppositeDirection" : true, "depth" : 3 * mm});
        }
        {
            var Q0;
            {var subQ0=sQuery(id+"F0.wireOp",EDGE,"E3");var subQ1=sQuery(id+"F0.wireOp",EDGE,"E1");var subQ2=makeQuery(id+"F0.imprint","INTERSECT",VERTEX,{"disambiguationData":[OD(1.0)],"derivedFrom":[subQ1,subQ0]});Q0=makeQuery(id+"F0.imprint","IMPRINT",FACE,{"disambiguationData":[TD([[makeQuery(id+"F0.imprint","IMPRINT",EDGE,{"disambiguationData":[TD([[subQ2,-1.0]])],"derivedFrom":subQ1}),1.0]])]});}
            var Q1;
            {var subQ0=sQuery(id+"F0.wireOp",EDGE,"E2");var subQ1=sQuery(id+"F0.wireOp",EDGE,"E1");var subQ2=makeQuery(id+"F0.imprint","INTERSECT",VERTEX,{"disambiguationData":[OD(0.0)],"derivedFrom":[subQ1,subQ0]});Q1=makeQuery(id+"F0.imprint","IMPRINT",FACE,{"disambiguationData":[TD([[makeQuery(id+"F0.imprint","IMPRINT",EDGE,{"disambiguationData":[TD([[subQ2,-1.0]])],"derivedFrom":subQ1}),1.0]])]});}
            var Q2;
            {var subQ0=sQuery(id+"F0.wireOp",EDGE,"E3");var subQ1=sQuery(id+"F0.wireOp",EDGE,"E1");var subQ2=makeQuery(id+"F0.imprint","INTERSECT",VERTEX,{"disambiguationData":[OD(0.0)],"derivedFrom":[subQ1,subQ0]});Q2=makeQuery(id+"F0.imprint","IMPRINT",FACE,{"disambiguationData":[TD([[makeQuery(id+"F0.imprint","IMPRINT",EDGE,{"disambiguationData":[TD([[subQ2,1.0]])],"derivedFrom":subQ1}),1.0]])]});}
            var Q3;
            {var subQ0=sQuery(id+"F0.wireOp",EDGE,"E2");var subQ1=sQuery(id+"F0.wireOp",EDGE,"E1");var subQ2=makeQuery(id+"F0.imprint","INTERSECT",VERTEX,{"disambiguationData":[OD(0.0)],"derivedFrom":[subQ1,subQ0]});Q3=makeQuery(id+"F0.imprint","IMPRINT",FACE,{"disambiguationData":[TD([[makeQuery(id+"F0.imprint","IMPRINT",EDGE,{"disambiguationData":[TD([[subQ2,1.0]])],"derivedFrom":subQ1}),1.0]])]});}
            var Q4;
            {var subQ0=sQuery(id+"F0.wireOp",EDGE,"E20.MirrorCS");var subQ1=sQuery(id+"F0.wireOp",EDGE,"E16.MirrorCS");var subQ2=makeQuery(id+"F0.imprint","INTERSECT",VERTEX,{"derivedFrom":[subQ1,subQ0]});Q4=makeQuery(id+"F0.imprint","IMPRINT",FACE,{"disambiguationData":[TD([[makeQuery(id+"F0.imprint","IMPRINT",EDGE,{"disambiguationData":[TD([[subQ2,-1.0]])],"derivedFrom":subQ1}),-1.0]])]});}
            var Q5;
            {var subQ0=sQuery(id+"F0.wireOp",EDGE,"E22.MirrorC");var subQ1=sQuery(id+"F0.wireOp",EDGE,"E16.MirrorCS");var subQ2=makeQuery(id+"F0.imprint","INTERSECT",VERTEX,{"disambiguationData":[OD(0.0)],"derivedFrom":[subQ1,subQ0]});Q5=makeQuery(id+"F0.imprint","IMPRINT",FACE,{"disambiguationData":[TD([[makeQuery(id+"F0.imprint","IMPRINT",EDGE,{"disambiguationData":[TD([[subQ2,-1.0]])],"derivedFrom":subQ1}),-1.0]])]});}
            var Q6;
            {var subQ0=sQuery(id+"F0.wireOp",EDGE,"E22.MirrorC");var subQ1=sQuery(id+"F0.wireOp",EDGE,"E16.MirrorCS");var subQ2=makeQuery(id+"F0.imprint","INTERSECT",VERTEX,{"disambiguationData":[OD(0.0)],"derivedFrom":[subQ1,subQ0]});Q6=makeQuery(id+"F0.imprint","IMPRINT",FACE,{"disambiguationData":[TD([[makeQuery(id+"F0.imprint","IMPRINT",EDGE,{"disambiguationData":[TD([[subQ2,-1.0]])],"derivedFrom":subQ1}),1.0]])]});}
            var Q7;
            {var subQ0=sQuery(id+"F0.wireOp",EDGE,"E20.MirrorCS");var subQ1=sQuery(id+"F0.wireOp",EDGE,"E16.MirrorCS");var subQ2=makeQuery(id+"F0.imprint","INTERSECT",VERTEX,{"derivedFrom":[subQ1,subQ0]});Q7=makeQuery(id+"F0.imprint","IMPRINT",FACE,{"disambiguationData":[TD([[makeQuery(id+"F0.imprint","IMPRINT",EDGE,{"disambiguationData":[TD([[subQ2,-1.0]])],"derivedFrom":subQ1}),1.0]])]});}
            var Q8;
            {var subQ0=sQuery(id+"F0.wireOp",EDGE,"E4");var subQ1=sQuery(id+"F0.wireOp",EDGE,"E3");var subQ2=makeQuery(id+"F0.imprint","INTERSECT",VERTEX,{"derivedFrom":[subQ1,subQ0]});Q8=makeQuery(id+"F0.imprint","IMPRINT",FACE,{"disambiguationData":[TD([[makeQuery(id+"F0.imprint","IMPRINT",EDGE,{"disambiguationData":[TD([[subQ2,-1.0]])],"derivedFrom":subQ1}),1.0]])]});}
            var Q9;
            {var subQ0=sQuery(id+"F0.wireOp",EDGE,"E8");var subQ1=sQuery(id+"F0.wireOp",EDGE,"E3");var subQ2=makeQuery(id+"F0.imprint","INTERSECT",VERTEX,{"disambiguationData":[OD(0.0)],"derivedFrom":[subQ1,subQ0]});Q9=makeQuery(id+"F0.imprint","IMPRINT",FACE,{"disambiguationData":[TD([[makeQuery(id+"F0.imprint","IMPRINT",EDGE,{"disambiguationData":[TD([[subQ2,-1.0]])],"derivedFrom":subQ1}),1.0]])]});}
            var Q10;
            {var subQ0=sQuery(id+"F0.wireOp",EDGE,"E8");var subQ1=sQuery(id+"F0.wireOp",EDGE,"E3");var subQ2=makeQuery(id+"F0.imprint","INTERSECT",VERTEX,{"disambiguationData":[OD(0.0)],"derivedFrom":[subQ1,subQ0]});Q10=makeQuery(id+"F0.imprint","IMPRINT",FACE,{"disambiguationData":[TD([[makeQuery(id+"F0.imprint","IMPRINT",EDGE,{"disambiguationData":[TD([[subQ2,-1.0]])],"derivedFrom":subQ1}),-1.0]])]});}
            var Q11;
            {var subQ0=sQuery(id+"F0.wireOp",EDGE,"E4");var subQ1=sQuery(id+"F0.wireOp",EDGE,"E3");var subQ2=makeQuery(id+"F0.imprint","INTERSECT",VERTEX,{"derivedFrom":[subQ1,subQ0]});Q11=makeQuery(id+"F0.imprint","IMPRINT",FACE,{"disambiguationData":[TD([[makeQuery(id+"F0.imprint","IMPRINT",EDGE,{"disambiguationData":[TD([[subQ2,-1.0]])],"derivedFrom":subQ1}),-1.0]])]});}
            var Q12;
            {var subQ0=sQuery(id+"F0.wireOp",EDGE,"E20.MirrorCS");var subQ1=sQuery(id+"F0.wireOp",EDGE,"E18.MirrorCS");var subQ2=makeQuery(id+"F0.imprint","INTERSECT",VERTEX,{"derivedFrom":[subQ1,subQ0]});Q12=makeQuery(id+"F0.imprint","IMPRINT",FACE,{"disambiguationData":[TD([[makeQuery(id+"F0.imprint","IMPRINT",EDGE,{"disambiguationData":[TD([[subQ2,-1.0]])],"derivedFrom":subQ1}),1.0]])]});}
            var Q13;
            {var subQ0=sQuery(id+"F0.wireOp",EDGE,"E24.MirrorC");var subQ1=sQuery(id+"F0.wireOp",EDGE,"E18.MirrorCS");var subQ2=makeQuery(id+"F0.imprint","INTERSECT",VERTEX,{"disambiguationData":[OD(0.0)],"derivedFrom":[subQ1,subQ0]});Q13=makeQuery(id+"F0.imprint","IMPRINT",FACE,{"disambiguationData":[TD([[makeQuery(id+"F0.imprint","IMPRINT",EDGE,{"disambiguationData":[TD([[subQ2,-1.0]])],"derivedFrom":subQ1}),1.0]])]});}
            var Q14;
            {var subQ0=sQuery(id+"F0.wireOp",EDGE,"E24.MirrorC");var subQ1=sQuery(id+"F0.wireOp",EDGE,"E18.MirrorCS");var subQ2=makeQuery(id+"F0.imprint","INTERSECT",VERTEX,{"disambiguationData":[OD(0.0)],"derivedFrom":[subQ1,subQ0]});Q14=makeQuery(id+"F0.imprint","IMPRINT",FACE,{"disambiguationData":[TD([[makeQuery(id+"F0.imprint","IMPRINT",EDGE,{"disambiguationData":[TD([[subQ2,-1.0]])],"derivedFrom":subQ1}),-1.0]])]});}
            var Q15;
            {var subQ0=sQuery(id+"F0.wireOp",EDGE,"E20.MirrorCS");var subQ1=sQuery(id+"F0.wireOp",EDGE,"E18.MirrorCS");var subQ2=makeQuery(id+"F0.imprint","INTERSECT",VERTEX,{"derivedFrom":[subQ1,subQ0]});Q15=makeQuery(id+"F0.imprint","IMPRINT",FACE,{"disambiguationData":[TD([[makeQuery(id+"F0.imprint","IMPRINT",EDGE,{"disambiguationData":[TD([[subQ2,-1.0]])],"derivedFrom":subQ1}),-1.0]])]});}
            var Q16;
            {var subQ0=sQuery(id+"F0.wireOp",EDGE,"E11");var subQ1=sQuery(id+"F0.wireOp",EDGE,"E3");var subQ2=makeQuery(id+"F0.imprint","INTERSECT",VERTEX,{"disambiguationData":[OD(0.0)],"derivedFrom":[subQ1,subQ0]});Q16=makeQuery(id+"F0.imprint","IMPRINT",FACE,{"disambiguationData":[TD([[makeQuery(id+"F0.imprint","IMPRINT",EDGE,{"disambiguationData":[TD([[subQ2,-1.0]])],"derivedFrom":subQ1}),-1.0]])]});}
            var Q17;
            {var subQ0=sQuery(id+"F0.wireOp",EDGE,"E11");var subQ1=sQuery(id+"F0.wireOp",EDGE,"E3");var subQ2=makeQuery(id+"F0.imprint","INTERSECT",VERTEX,{"disambiguationData":[OD(0.0)],"derivedFrom":[subQ1,subQ0]});Q17=makeQuery(id+"F0.imprint","IMPRINT",FACE,{"disambiguationData":[TD([[makeQuery(id+"F0.imprint","IMPRINT",EDGE,{"disambiguationData":[TD([[subQ2,-1.0]])],"derivedFrom":subQ1}),1.0]])]});}
            var Q18;
            {var subQ0=sQuery(id+"F0.wireOp",EDGE,"E7");var subQ1=sQuery(id+"F0.wireOp",EDGE,"E3");var subQ2=makeQuery(id+"F0.imprint","INTERSECT",VERTEX,{"derivedFrom":[subQ1,subQ0]});Q18=makeQuery(id+"F0.imprint","IMPRINT",FACE,{"disambiguationData":[TD([[makeQuery(id+"F0.imprint","IMPRINT",EDGE,{"disambiguationData":[TD([[subQ2,-1.0]])],"derivedFrom":subQ1}),1.0]])]});}
            var Q19;
            {var subQ0=sQuery(id+"F0.wireOp",EDGE,"E7");var subQ1=sQuery(id+"F0.wireOp",EDGE,"E3");var subQ2=makeQuery(id+"F0.imprint","INTERSECT",VERTEX,{"derivedFrom":[subQ1,subQ0]});Q19=makeQuery(id+"F0.imprint","IMPRINT",FACE,{"disambiguationData":[TD([[makeQuery(id+"F0.imprint","IMPRINT",EDGE,{"disambiguationData":[TD([[subQ2,-1.0]])],"derivedFrom":subQ1}),-1.0]])]});}
            extrude(context, id + "F2", {"entities" : qUnion([Q0, Q1, Q2, Q3, Q4, Q5, Q6, Q7, Q8, Q9, Q10, Q11, Q12, Q13, Q14, Q15, Q16, Q17, Q18, Q19]), "operationType" : NewBodyOperationType.ADD, "depth" : 5 * mm});
        }
        {
            var Q0;
            Q0=makeQuery(id+"F1.opExtrude","SWEPT_FACE",FACE,{"disambiguationData":[OSD([sQuery(id+"F0.wireOp",EDGE,"E0.right"),sQuery(id+"F0.wireOp",EDGE,"E14")])]});
            var Q1;
            Q1=makeQuery(id+"F1.opExtrude","SWEPT_FACE",FACE,{"disambiguationData":[OSD([sQuery(id+"F0.wireOp",EDGE,"E13")])]});
            var Q2;
            Q2=makeQuery(id+"F1.opExtrude","SWEPT_FACE",FACE,{"disambiguationData":[OSD([sQuery(id+"F0.wireOp",EDGE,"E0.bottom")])]});
            var Q3;
            Q3=makeQuery(id+"F1.opExtrude","SWEPT_FACE",FACE,{"disambiguationData":[OSD([sQuery(id+"F0.wireOp",EDGE,"E0.left"),sQuery(id+"F0.wireOp",EDGE,"E12")])]});
            fillet(context, id + "F3", {"entities" : qUnion([Q0, Q1, Q2, Q3]), "radius" : 1 * mm, "tangentPropagation" : true, "allowEdgeOverflow" : false});
        }
        {
            var Q0;
            {var subQ0=sQuery(id+"F0.wireOp",EDGE,"E43.MirrorC");var subQ1=makeQuery(id+"F0.imprint","INTERSECT",VERTEX,{"derivedFrom":[subQ0,sQuery(id+"F0.wireOp",EDGE,"E64.trimOffspring")]});Q0=makeQuery(id+"F0.imprint","IMPRINT",FACE,{"disambiguationData":[TD([[makeQuery(id+"F0.imprint","IMPRINT",EDGE,{"disambiguationData":[TD([[subQ1,-1.0]])],"derivedFrom":subQ0}),-1.0]])]});}
            var Q1;
            {var subQ0=sQuery(id+"F0.wireOp",EDGE,"E49.MirrorC");var subQ1=makeQuery(id+"F0.imprint","INTERSECT",VERTEX,{"derivedFrom":[sQuery(id+"F0.wireOp",EDGE,"E34.MirrorCS"),subQ0]});Q1=makeQuery(id+"F0.imprint","IMPRINT",FACE,{"disambiguationData":[TD([[makeQuery(id+"F0.imprint","IMPRINT",EDGE,{"disambiguationData":[TD([[subQ1,1.0]])],"derivedFrom":subQ0}),1.0]])]});}
            var Q2;
            {var subQ0=sQuery(id+"F0.wireOp",EDGE,"E46.MirrorC");var subQ1=makeQuery(id+"F0.imprint","INTERSECT",VERTEX,{"derivedFrom":[subQ0,sQuery(id+"F0.wireOp",EDGE,"E62.trimOffspring")]});Q2=makeQuery(id+"F0.imprint","IMPRINT",FACE,{"disambiguationData":[TD([[makeQuery(id+"F0.imprint","IMPRINT",EDGE,{"disambiguationData":[TD([[subQ1,1.0]])],"derivedFrom":subQ0}),-1.0]])]});}
            var Q3;
            {var subQ0=sQuery(id+"F0.wireOp",EDGE,"E47.MirrorC");var subQ1=makeQuery(id+"F0.imprint","INTERSECT",VERTEX,{"derivedFrom":[sQuery(id+"F0.wireOp",EDGE,"E36.MirrorCS"),subQ0]});Q3=makeQuery(id+"F0.imprint","IMPRINT",FACE,{"disambiguationData":[TD([[makeQuery(id+"F0.imprint","IMPRINT",EDGE,{"disambiguationData":[TD([[subQ1,1.0]])],"derivedFrom":subQ0}),1.0]])]});}
            var Q4;
            {var subQ0=sQuery(id+"F0.wireOp",EDGE,"E51.MirrorC");var subQ1=makeQuery(id+"F0.imprint","INTERSECT",VERTEX,{"derivedFrom":[sQuery(id+"F0.wireOp",EDGE,"E29.MirrorCS"),subQ0]});Q4=makeQuery(id+"F0.imprint","IMPRINT",FACE,{"disambiguationData":[TD([[makeQuery(id+"F0.imprint","IMPRINT",EDGE,{"disambiguationData":[TD([[subQ1,1.0]])],"derivedFrom":subQ0}),1.0]])]});}
            extrude(context, id + "F4", {"entities" : qUnion([Q0, Q1, Q2, Q3, Q4]), "depth" : 5 * mm});
        }
        {
            var Q0;
            {var subQ0=sQuery(id+"F0.wireOp",EDGE,"E64.trimOffspring");Q0=makeQuery(id+"F0.imprint","IMPRINT",FACE,{"disambiguationData":[TD([[makeQuery(id+"F0.imprint","IMPRINT",EDGE,{"derivedFrom":subQ0}),-1.0]])]});}
            var Q1;
            {var subQ1=sQuery(id+"F0.wireOp",EDGE,"E36.MirrorCS");Q1=makeQuery(id+"F0.imprint","IMPRINT",FACE,{"disambiguationData":[TD([[makeQuery(id+"F0.imprint","IMPRINT",EDGE,{"derivedFrom":subQ1}),1.0]])]});}
            var Q2;
            {var subQ0=sQuery(id+"F0.wireOp",EDGE,"E54.trimOffspring");Q2=makeQuery(id+"F0.imprint","IMPRINT",FACE,{"disambiguationData":[TD([[makeQuery(id+"F0.imprint","IMPRINT",EDGE,{"derivedFrom":subQ0}),-1.0]])]});}
            var Q3;
            {var subQ2=sQuery(id+"F0.wireOp",EDGE,"E29.MirrorCS");Q3=makeQuery(id+"F0.imprint","IMPRINT",FACE,{"disambiguationData":[TD([[makeQuery(id+"F0.imprint","IMPRINT",EDGE,{"derivedFrom":subQ2}),1.0]])]});}
            var Q4;
            {var subQ0=sQuery(id+"F0.wireOp",EDGE,"E58.trimOffspring");Q4=makeQuery(id+"F0.imprint","IMPRINT",FACE,{"disambiguationData":[TD([[makeQuery(id+"F0.imprint","IMPRINT",EDGE,{"derivedFrom":subQ0}),-1.0]])]});}
            var Q5;
            {var subQ0=sQuery(id+"F0.wireOp",EDGE,"E41.MirrorCS");var subQ1=sQuery(id+"F0.wireOp",EDGE,"E26.MirrorCS");var subQ2=makeQuery(id+"F0.imprint","INTERSECT",VERTEX,{"derivedFrom":[subQ1,subQ0]});Q5=makeQuery(id+"F0.imprint","IMPRINT",FACE,{"disambiguationData":[TD([[makeQuery(id+"F0.imprint","IMPRINT",EDGE,{"disambiguationData":[TD([[subQ2,1.0]])],"derivedFrom":subQ1}),-1.0]])]});}
            var Q6;
            {var subQ0=sQuery(id+"F0.wireOp",EDGE,"E49.MirrorC");var subQ1=makeQuery(id+"F0.imprint","INTERSECT",VERTEX,{"derivedFrom":[sQuery(id+"F0.wireOp",EDGE,"E34.MirrorCS"),subQ0]});Q6=makeQuery(id+"F0.imprint","IMPRINT",FACE,{"disambiguationData":[TD([[makeQuery(id+"F0.imprint","IMPRINT",EDGE,{"disambiguationData":[TD([[subQ1,1.0]])],"derivedFrom":subQ0}),1.0]])]});}
            var Q7;
            {var subQ0=sQuery(id+"F0.wireOp",EDGE,"E56.trimOffspring");Q7=makeQuery(id+"F0.imprint","IMPRINT",FACE,{"disambiguationData":[TD([[makeQuery(id+"F0.imprint","IMPRINT",EDGE,{"derivedFrom":subQ0}),-1.0]])]});}
            var Q8;
            {var subQ3=sQuery(id+"F0.wireOp",EDGE,"E29.MirrorCS");Q8=makeQuery(id+"F0.imprint","IMPRINT",FACE,{"disambiguationData":[TD([[makeQuery(id+"F0.imprint","IMPRINT",EDGE,{"derivedFrom":subQ3}),-1.0]])]});}
            var Q9;
            {var subQ9=sQuery(id+"F0.wireOp",EDGE,"E63.trimOffspring");Q9=makeQuery(id+"F0.imprint","IMPRINT",FACE,{"disambiguationData":[TD([[makeQuery(id+"F0.imprint","IMPRINT",EDGE,{"derivedFrom":subQ9}),1.0]])]});}
            var Q10;
            {var subQ3=sQuery(id+"F0.wireOp",EDGE,"E34.MirrorCS");Q10=makeQuery(id+"F0.imprint","IMPRINT",FACE,{"disambiguationData":[TD([[makeQuery(id+"F0.imprint","IMPRINT",EDGE,{"derivedFrom":subQ3}),1.0]])]});}
            var Q11;
            {var subQ0=sQuery(id+"F0.wireOp",EDGE,"E43.MirrorC");var subQ1=makeQuery(id+"F0.imprint","INTERSECT",VERTEX,{"derivedFrom":[subQ0,sQuery(id+"F0.wireOp",EDGE,"E64.trimOffspring")]});Q11=makeQuery(id+"F0.imprint","IMPRINT",FACE,{"disambiguationData":[TD([[makeQuery(id+"F0.imprint","IMPRINT",EDGE,{"disambiguationData":[TD([[subQ1,-1.0]])],"derivedFrom":subQ0}),-1.0]])]});}
            var Q12;
            {var subQ0=sQuery(id+"F0.wireOp",EDGE,"E46.MirrorC");var subQ1=makeQuery(id+"F0.imprint","INTERSECT",VERTEX,{"derivedFrom":[subQ0,sQuery(id+"F0.wireOp",EDGE,"E62.trimOffspring")]});Q12=makeQuery(id+"F0.imprint","IMPRINT",FACE,{"disambiguationData":[TD([[makeQuery(id+"F0.imprint","IMPRINT",EDGE,{"disambiguationData":[TD([[subQ1,1.0]])],"derivedFrom":subQ0}),-1.0]])]});}
            var Q13;
            {var subQ3=sQuery(id+"F0.wireOp",EDGE,"E35.MirrorCS");Q13=makeQuery(id+"F0.imprint","IMPRINT",FACE,{"disambiguationData":[TD([[makeQuery(id+"F0.imprint","IMPRINT",EDGE,{"derivedFrom":subQ3}),1.0]])]});}
            var Q14;
            {var subQ4=sQuery(id+"F0.wireOp",EDGE,"E65.trimOffspring");Q14=makeQuery(id+"F0.imprint","IMPRINT",FACE,{"disambiguationData":[TD([[makeQuery(id+"F0.imprint","IMPRINT",EDGE,{"derivedFrom":subQ4}),-1.0]])]});}
            var Q15;
            {var subQ0=sQuery(id+"F0.wireOp",EDGE,"E60.trimOffspring");Q15=makeQuery(id+"F0.imprint","IMPRINT",FACE,{"disambiguationData":[TD([[makeQuery(id+"F0.imprint","IMPRINT",EDGE,{"derivedFrom":subQ0}),1.0]])]});}
            var Q16;
            {var subQ0=sQuery(id+"F0.wireOp",EDGE,"E52.trimOffspring");Q16=makeQuery(id+"F0.imprint","IMPRINT",FACE,{"disambiguationData":[TD([[makeQuery(id+"F0.imprint","IMPRINT",EDGE,{"derivedFrom":subQ0}),-1.0]])]});}
            var Q17;
            {var subQ0=sQuery(id+"F0.wireOp",EDGE,"E71.trimOffspring");Q17=makeQuery(id+"F0.imprint","IMPRINT",FACE,{"disambiguationData":[TD([[makeQuery(id+"F0.imprint","IMPRINT",EDGE,{"derivedFrom":subQ0}),-1.0]])]});}
            var Q18;
            {var subQ0=sQuery(id+"F0.wireOp",EDGE,"E32.MirrorCS");var subQ7=sQuery(id+"F0.wireOp",EDGE,"E26.MirrorCS");var subQ8=makeQuery(id+"F0.imprint","INTERSECT",VERTEX,{"derivedFrom":[subQ7,subQ0]});Q18=makeQuery(id+"F0.imprint","IMPRINT",FACE,{"disambiguationData":[TD([[makeQuery(id+"F0.imprint","IMPRINT",EDGE,{"disambiguationData":[TD([[subQ8,-1.0]])],"derivedFrom":subQ7}),-1.0]])]});}
            var Q19;
            {var subQ7=sQuery(id+"F0.wireOp",EDGE,"E58.trimOffspring");Q19=makeQuery(id+"F0.imprint","IMPRINT",FACE,{"disambiguationData":[TD([[makeQuery(id+"F0.imprint","IMPRINT",EDGE,{"derivedFrom":subQ7}),1.0]])]});}
            var Q20;
            {var subQ0=sQuery(id+"F0.wireOp",EDGE,"E52.trimOffspring");Q20=makeQuery(id+"F0.imprint","IMPRINT",FACE,{"disambiguationData":[TD([[makeQuery(id+"F0.imprint","IMPRINT",EDGE,{"derivedFrom":subQ0}),1.0]])]});}
            var Q21;
            {var subQ0=sQuery(id+"F0.wireOp",EDGE,"E51.MirrorC");var subQ1=makeQuery(id+"F0.imprint","INTERSECT",VERTEX,{"derivedFrom":[sQuery(id+"F0.wireOp",EDGE,"E29.MirrorCS"),subQ0]});Q21=makeQuery(id+"F0.imprint","IMPRINT",FACE,{"disambiguationData":[TD([[makeQuery(id+"F0.imprint","IMPRINT",EDGE,{"disambiguationData":[TD([[subQ1,1.0]])],"derivedFrom":subQ0}),1.0]])]});}
            var Q22;
            {var subQ7=sQuery(id+"F0.wireOp",EDGE,"E59.trimOffspring");Q22=makeQuery(id+"F0.imprint","IMPRINT",FACE,{"disambiguationData":[TD([[makeQuery(id+"F0.imprint","IMPRINT",EDGE,{"derivedFrom":subQ7}),-1.0]])]});}
            var Q23;
            {var subQ0=sQuery(id+"F0.wireOp",EDGE,"E61.trimOffspring");Q23=makeQuery(id+"F0.imprint","IMPRINT",FACE,{"disambiguationData":[TD([[makeQuery(id+"F0.imprint","IMPRINT",EDGE,{"derivedFrom":subQ0}),1.0]])]});}
            var Q24;
            {var subQ9=sQuery(id+"F0.wireOp",EDGE,"E62.trimOffspring");Q24=makeQuery(id+"F0.imprint","IMPRINT",FACE,{"disambiguationData":[TD([[makeQuery(id+"F0.imprint","IMPRINT",EDGE,{"derivedFrom":subQ9}),-1.0]])]});}
            var Q25;
            {var subQ0=sQuery(id+"F0.wireOp",EDGE,"E47.MirrorC");var subQ1=makeQuery(id+"F0.imprint","INTERSECT",VERTEX,{"derivedFrom":[sQuery(id+"F0.wireOp",EDGE,"E36.MirrorCS"),subQ0]});Q25=makeQuery(id+"F0.imprint","IMPRINT",FACE,{"disambiguationData":[TD([[makeQuery(id+"F0.imprint","IMPRINT",EDGE,{"disambiguationData":[TD([[subQ1,1.0]])],"derivedFrom":subQ0}),1.0]])]});}
            extrude(context, id + "F5", {"entities" : qUnion([Q0, Q1, Q2, Q3, Q4, Q5, Q6, Q7, Q8, Q9, Q10, Q11, Q12, Q13, Q14, Q15, Q16, Q17, Q18, Q19, Q20, Q21, Q22, Q23, Q24, Q25]), "oppositeDirection" : true, "depth" : 3 * mm});
        }
        {
            var Q0;
            Q0=makeQuery(id+"F5.opExtrude","SWEPT_FACE",FACE,{"disambiguationData":[OSD([sQuery(id+"F0.wireOp",EDGE,"E0.left"),sQuery(id+"F0.wireOp",EDGE,"E12")])]});
            var Q1;
            Q1=makeQuery(id+"F5.opExtrude","SWEPT_FACE",FACE,{"disambiguationData":[OSD([sQuery(id+"F0.wireOp",EDGE,"E28.MirrorCS")])]});
            var Q2;
            Q2=makeQuery(id+"F5.opExtrude","SWEPT_FACE",FACE,{"disambiguationData":[OSD([sQuery(id+"F0.wireOp",EDGE,"E31.MirrorCS"),sQuery(id+"F0.wireOp",EDGE,"E32.MirrorCS")])]});
            var Q3;
            Q3=makeQuery(id+"F5.opExtrude","SWEPT_FACE",FACE,{"disambiguationData":[OSD([sQuery(id+"F0.wireOp",EDGE,"E30.MirrorCS")])]});
            fillet(context, id + "F6", {"entities" : qUnion([Q0, Q1, Q2, Q3]), "radius" : 1 * mm, "tangentPropagation" : true, "allowEdgeOverflow" : false});
        }
        {
            var Q0;
            Q0=makeQuery(id+"F4.opExtrude","CAP_EDGE",EDGE,{"disambiguationData":[OSD([sQuery(id+"F0.wireOp",EDGE,"E47.MirrorC")])],"isStart":false});
            var Q1;
            Q1=makeQuery(id+"F4.opExtrude","CAP_EDGE",EDGE,{"disambiguationData":[OSD([sQuery(id+"F0.wireOp",EDGE,"E46.MirrorC")])],"isStart":false});
            fillet(context, id + "F7", {"entities" : qUnion([Q0, Q1]), "radius" : 1 * mm, "tangentPropagation" : true, "allowEdgeOverflow" : false});
        }
    });
